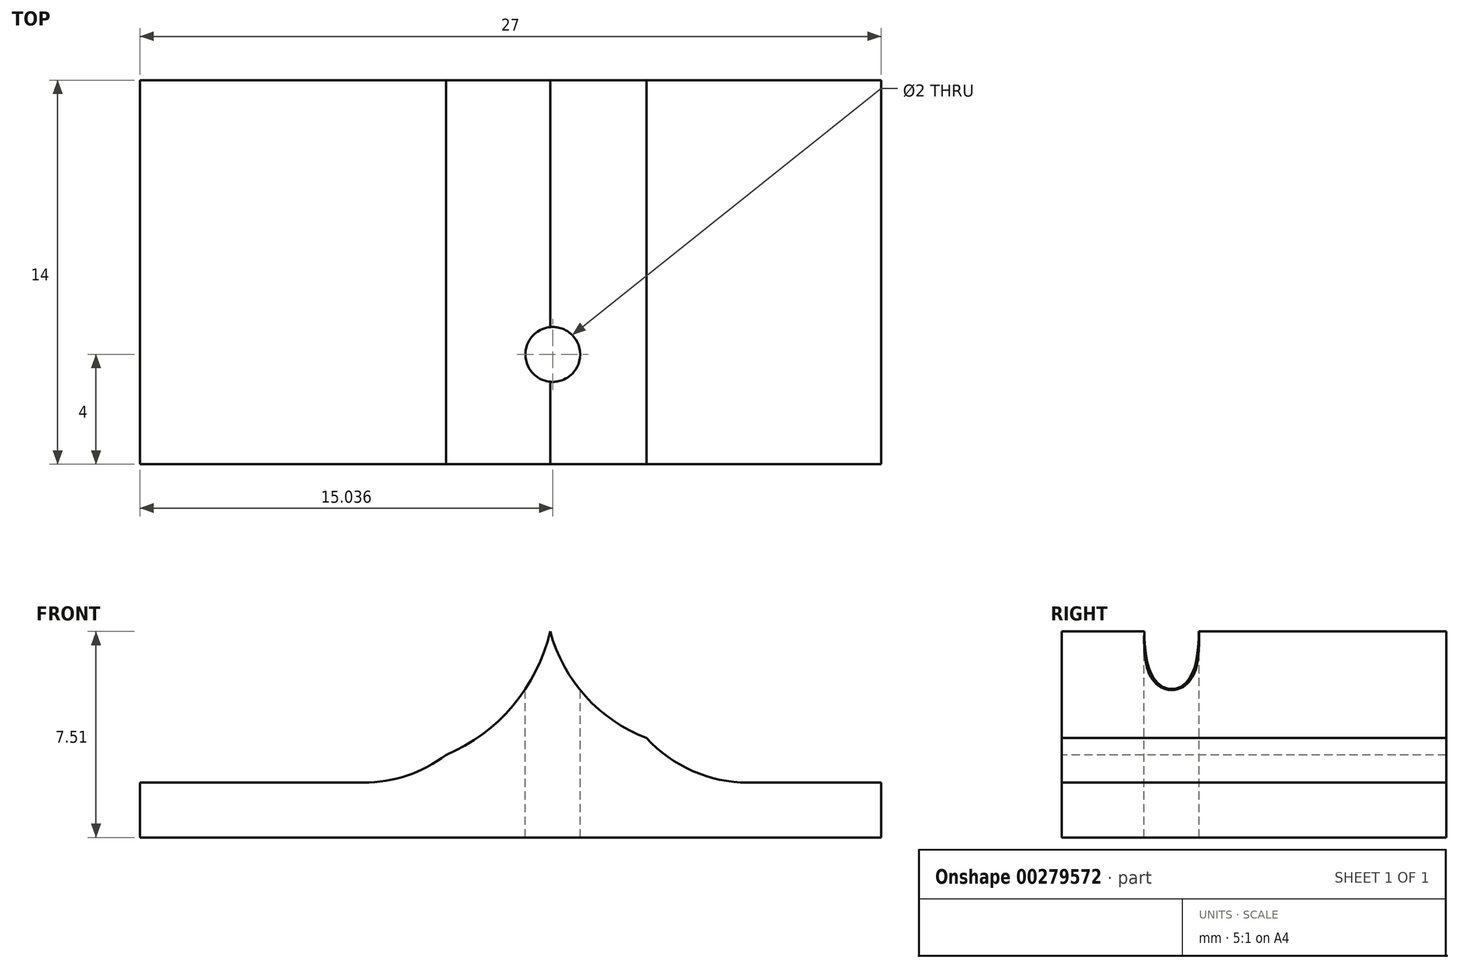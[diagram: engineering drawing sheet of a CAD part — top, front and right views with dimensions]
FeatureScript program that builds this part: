
annotation { "Feature Type Name" : "Feature", "Feature Type Description" : "" }
export const myFeature = defineFeature(function(context is Context, id is Id, definition is map)
    precondition{}
    {
        {
            var Q0;
            Q0=qCreatedBy(makeId("Front.planeOp"),FACE);
            var sketch = newSketch(context, id + "F0", { "sketchPlane" : qUnion([Q0])});
            skLineSegment(sketch, "E0", {"start": v(-27, 2) * mm, "end": v(-27, 0) * mm});
            skLineSegment(sketch, "E1", {"start": v(-27, 0) * mm, "end": v(0, 0) * mm});
            skLineSegment(sketch, "E2", {"start": v(0, 0) * mm, "end": v(0, 2) * mm});
            skLineSegment(sketch, "E3", {"start": v(-12, 9) * mm, "end": v(-12, 2) * mm});
            skLineSegment(sketch, "E4", {"start": v(-12, 2) * mm, "end": v(-7.5, 2) * mm});
            skLineSegment(sketch, "E5", {"start": v(-7.5, 2) * mm, "end": v(-12, 9) * mm});
            skLineSegment(sketch, "E6", {"start": v(-27, 2) * mm, "end": v(-12, 2) * mm});
            skLineSegment(sketch, "E7.top", {"start": v(-12, 2) * mm, "end": v(-16.5, 2) * mm});
            skLineSegment(sketch, "E8", {"start": v(-12, 9) * mm, "end": v(-16.5, 2) * mm});
            skLineSegment(sketch, "E9", {"start": v(-7.5, 2) * mm, "end": v(0, 2) * mm});
            skSolve(sketch);
        }
        {
            var Q0;
            Q0 = qSketchRegion(id + "F0", true);
            extrude(context, id + "F1", {"entities" : qUnion([Q0]), "depth" : 14 * mm});
        }
        {
            var Q0;
            Q0=makeQuery(id+"F1.opExtrude","SWEPT_EDGE",EDGE,{"disambiguationData":[OSD([sQuery(id+"F0.wireOp",EDGE,"E5"),sQuery(id+"F0.wireOp",EDGE,"E3"),sQuery(id+"F0.wireOp",EDGE,"E8")])]});
            cPlane(context, id + "F2", {"entities" : qUnion([Q0]), "cplaneType" : CPlaneType.LINE_ANGLE, "offset" : 25 * mm, "angle" : 0 * degree, "width" : 150 * mm, "height" : 150 * mm});
        }
        {
            var Q0;
            Q0=qCreatedBy(id+"F2.planeOp",FACE);
            var sketch = newSketch(context, id + "F3", { "sketchPlane" : qUnion([Q0])});
            skLineSegment(sketch, "E10", {"start": v(-11.96, 0) * mm, "end": v(-11.96, -15) * mm});
            skLineSegment(sketch, "E11", {"start": v(-11.96, 0) * mm, "end": v(-11.96, -10) * mm});
            skCircle(sketch, "E12", {"center": v(-11.96, -10) * mm, "radius": 1 * mm});
            skSolve(sketch);
        }
        {
            var Q0;
            Q0 = qSketchRegion(id + "F3", true);
            extrude(context, id + "F4", {"entities" : qUnion([Q0]), "operationType" : NewBodyOperationType.REMOVE, "oppositeDirection" : true, "depth" : 25 * mm});
        }
        {
            var Q0;
            Q0=makeQuery(id+"F1.opExtrude","CAP_FACE",FACE,{"disambiguationData":[OSD([sQuery(id+"F0.wireOp",EDGE,"E0"),sQuery(id+"F0.wireOp",EDGE,"E1"),sQuery(id+"F0.wireOp",EDGE,"E2"),sQuery(id+"F0.wireOp",EDGE,"E5"),sQuery(id+"F0.wireOp",EDGE,"E6"),sQuery(id+"F0.wireOp",EDGE,"E8"),sQuery(id+"F0.wireOp",EDGE,"E9")])],"isStart":false});
            cPlane(context, id + "F5", {"entities" : qUnion([Q0]), "cplaneType" : CPlaneType.OFFSET, "offset" : 0 * mm, "width" : 150 * mm, "height" : 150 * mm});
        }
        {
            var Q0;
            Q0=qCreatedBy(id+"F5.planeOp",FACE);
            var sketch = newSketch(context, id + "F6", { "sketchPlane" : qUnion([Q0])});
            skLineSegment(sketch, "E13", {"start": v(-12, 9) * mm, "end": v(-18.4, 9) * mm});
            skLineSegment(sketch, "E14", {"start": v(-12, 9) * mm, "end": v(-6.5, 9) * mm});
            skCircle(sketch, "E15", {"center": v(-18.4, 9) * mm, "radius": 6.51 * mm});
            skCircle(sketch, "E16", {"center": v(-6.5, 9) * mm, "radius": 5.75 * mm});
            skSolve(sketch);
        }
        {
            var Q0;
            Q0 = qSketchRegion(id + "F6", true);
            extrude(context, id + "F7", {"entities" : qUnion([Q0]), "operationType" : NewBodyOperationType.REMOVE, "oppositeDirection" : true, "depth" : 25 * mm});
        }
        {
            var Q0;
            Q0=makeQuery(id+"F1.opExtrude","SWEPT_EDGE",EDGE,{"disambiguationData":[OSD([sQuery(id+"F0.wireOp",EDGE,"E6"),sQuery(id+"F0.wireOp",EDGE,"E7.top"),sQuery(id+"F0.wireOp",EDGE,"E8")])]});
            fillet(context, id + "F8", {"entities" : qUnion([Q0]), "radius" : 5 * mm, "tangentPropagation" : true, "allowEdgeOverflow" : false});
        }
        {
            var Q0;
            Q0=makeQuery(id+"F1.opExtrude","SWEPT_EDGE",EDGE,{"disambiguationData":[OSD([sQuery(id+"F0.wireOp",EDGE,"E4"),sQuery(id+"F0.wireOp",EDGE,"E5"),sQuery(id+"F0.wireOp",EDGE,"E9")])]});
            fillet(context, id + "F9", {"entities" : qUnion([Q0]), "radius" : 5 * mm, "tangentPropagation" : true, "allowEdgeOverflow" : false});
        }
    });
